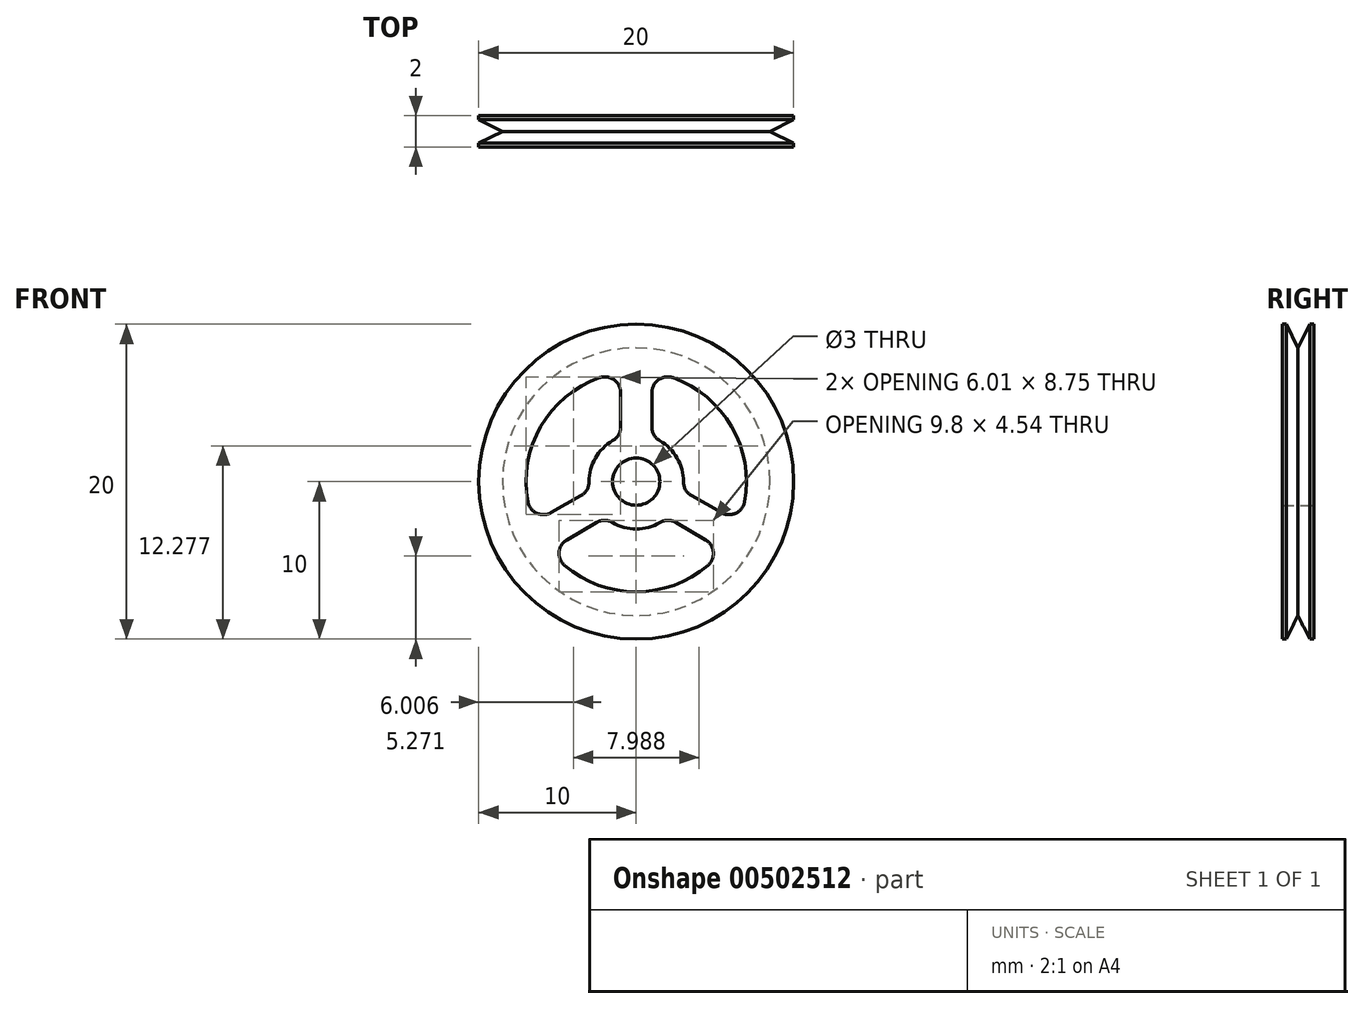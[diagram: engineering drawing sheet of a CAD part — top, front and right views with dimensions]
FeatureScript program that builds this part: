
annotation { "Feature Type Name" : "Feature", "Feature Type Description" : "" }
export const myFeature = defineFeature(function(context is Context, id is Id, definition is map)
    precondition{}
    {
        {
            var Q0;
            Q0=qCreatedBy(makeId("Front.planeOp"),FACE);
            var sketch = newSketch(context, id + "F0", { "sketchPlane" : qUnion([Q0])});
            skCircle(sketch, "E0", {"center": v(0, 0) * mm, "radius": 1.5 * mm});
            skArc(sketch, "E1", {"start": v(-1.5, -2.6) * mm, "mid": v(0, -3) * mm, "end": v(1.5, -2.6) * mm});
            skArc(sketch, "E2", {"start": v(-2.33, 6.6) * mm, "mid": v(-6.06, 3.5) * mm, "end": v(-6.88, -1.28) * mm});
            skCircle(sketch, "E3", {"center": v(0, 0) * mm, "radius": 10 * mm});
            skLineSegment(sketch, "E4.0", {"start": v(-0.99, 3.47) * mm, "end": v(-1, 5.66) * mm});
            skLineSegment(sketch, "E5.trimOffspring", {"start": v(0.99, 3.47) * mm, "end": v(1, 5.66) * mm});
            skLineSegment(sketch, "E6.1.0", {"start": v(-3.5, -0.88) * mm, "end": v(-5.4, -1.97) * mm});
            skLineSegment(sketch, "E6.1.1", {"start": v(-2.51, -2.6) * mm, "end": v(-4.4, -3.7) * mm});
            skLineSegment(sketch, "E6.2.0", {"start": v(2.51, -2.6) * mm, "end": v(4.4, -3.7) * mm});
            skLineSegment(sketch, "E6.2.1", {"start": v(3.5, -0.88) * mm, "end": v(5.4, -1.97) * mm});
            skArc(sketch, "E7.trimOffspring", {"start": v(-4.55, -5.32) * mm, "mid": v(0, -7) * mm, "end": v(4.55, -5.32) * mm});
            skArc(sketch, "E8.trimOffspring", {"start": v(-1.5, 2.6) * mm, "mid": v(-2.6, 1.5) * mm, "end": v(-3, -0.01) * mm});
            skArc(sketch, "E9.trimOffspring", {"start": v(3, -0.01) * mm, "mid": v(2.6, 1.5) * mm, "end": v(1.5, 2.6) * mm});
            skArc(sketch, "E10.trimOffspring", {"start": v(6.88, -1.28) * mm, "mid": v(6.06, 3.5) * mm, "end": v(2.33, 6.6) * mm});
            skPoint(sketch, "E11.visualSharp", {"position": v(-1, 6.93) * mm});
            skArc(sketch, "E11.filletArc", {"start": v(-1, 5.66) * mm, "mid": v(-1.42, 6.48) * mm, "end": v(-2.33, 6.6) * mm});
            skPoint(sketch, "E12.visualSharp", {"position": v(-0.99, 2.83) * mm});
            skArc(sketch, "E12.filletArc", {"start": v(-1.5, 2.6) * mm, "mid": v(-1.12, 2.97) * mm, "end": v(-0.99, 3.47) * mm});
            skPoint(sketch, "E13.visualSharp", {"position": v(-2.95, -0.56) * mm});
            skArc(sketch, "E13.filletArc", {"start": v(-3.5, -0.88) * mm, "mid": v(-3.13, -0.51) * mm, "end": v(-3, -0.01) * mm});
            skPoint(sketch, "E14.visualSharp", {"position": v(-6.5, -2.6) * mm});
            skArc(sketch, "E14.filletArc", {"start": v(-6.88, -1.28) * mm, "mid": v(-6.32, -2) * mm, "end": v(-5.4, -1.97) * mm});
            skPoint(sketch, "E15.visualSharp", {"position": v(-5.5, -4.33) * mm});
            skArc(sketch, "E15.filletArc", {"start": v(-4.4, -3.7) * mm, "mid": v(-4.9, -4.47) * mm, "end": v(-4.55, -5.32) * mm});
            skPoint(sketch, "E16.visualSharp", {"position": v(-1.96, -2.27) * mm});
            skArc(sketch, "E16.filletArc", {"start": v(-1.5, -2.6) * mm, "mid": v(-2.01, -2.46) * mm, "end": v(-2.51, -2.6) * mm});
            skPoint(sketch, "E17.visualSharp", {"position": v(1.96, -2.27) * mm});
            skArc(sketch, "E17.filletArc", {"start": v(2.51, -2.6) * mm, "mid": v(2.01, -2.46) * mm, "end": v(1.5, -2.6) * mm});
            skPoint(sketch, "E18.visualSharp", {"position": v(5.5, -4.33) * mm});
            skArc(sketch, "E18.filletArc", {"start": v(4.55, -5.32) * mm, "mid": v(4.9, -4.47) * mm, "end": v(4.4, -3.7) * mm});
            skPoint(sketch, "E19.visualSharp", {"position": v(6.5, -2.6) * mm});
            skArc(sketch, "E19.filletArc", {"start": v(5.4, -1.97) * mm, "mid": v(6.32, -2) * mm, "end": v(6.88, -1.28) * mm});
            skPoint(sketch, "E20.visualSharp", {"position": v(2.95, -0.56) * mm});
            skArc(sketch, "E20.filletArc", {"start": v(3, -0.01) * mm, "mid": v(3.13, -0.51) * mm, "end": v(3.5, -0.88) * mm});
            skPoint(sketch, "E21.visualSharp", {"position": v(0.99, 2.83) * mm});
            skArc(sketch, "E21.filletArc", {"start": v(0.99, 3.47) * mm, "mid": v(1.12, 2.97) * mm, "end": v(1.5, 2.6) * mm});
            skPoint(sketch, "E22.visualSharp", {"position": v(1, 6.93) * mm});
            skArc(sketch, "E22.filletArc", {"start": v(2.33, 6.6) * mm, "mid": v(1.42, 6.48) * mm, "end": v(1, 5.66) * mm});
            skSolve(sketch);
        }
        {
            var Q0;
            Q0=makeQuery(id+"F0.imprint","IMPRINT",FACE,{"disambiguationData":[TD([[makeQuery(id+"F0.imprint","IMPRINT",EDGE,{"derivedFrom":sQuery(id+"F0.wireOp",EDGE,"E0")}),-1.0]])]});
            extrude(context, id + "F1", {"entities" : qUnion([Q0]), "endBound" : BoundingType.SYMMETRIC, "depth" : 2 * mm});
        }
        {
            var Q0;
            Q0=qCreatedBy(makeId("Right.planeOp"),FACE);
            var sketch = newSketch(context, id + "F2", { "sketchPlane" : qUnion([Q0])});
            skLineSegment(sketch, "E23", {"start": v(0, 10) * mm, "end": v(0.75, 10) * mm});
            skLineSegment(sketch, "E24", {"start": v(0.75, 10) * mm, "end": v(0, 8.5) * mm});
            skLineSegment(sketch, "E25", {"start": v(0, 8.5) * mm, "end": v(0, 10) * mm});
            skLineSegment(sketch, "E26.MirrorCS", {"start": v(-0.75, 10) * mm, "end": v(0, 8.5) * mm});
            skLineSegment(sketch, "E27.MirrorCS", {"start": v(0, 10) * mm, "end": v(-0.75, 10) * mm});
            skLineSegment(sketch, "E28", {"start": v(2.2, 0) * mm, "end": v(-2.56, 0) * mm, "construction": true});
            skSolve(sketch);
        }
        {
            var Q0;
            Q0 = qSketchRegion(id + "F2", true);
            var Q1;
            Q1=sQuery(id+"F2.wireOp",EDGE,"E28");
            revolve(context, id + "F3", {"operationType" : NewBodyOperationType.REMOVE, "entities" : qUnion([Q0]), "axis" : qUnion([Q1]), "revolveType" : RevolveType.FULL, "oppositeDirection" : true});
        }
    });
